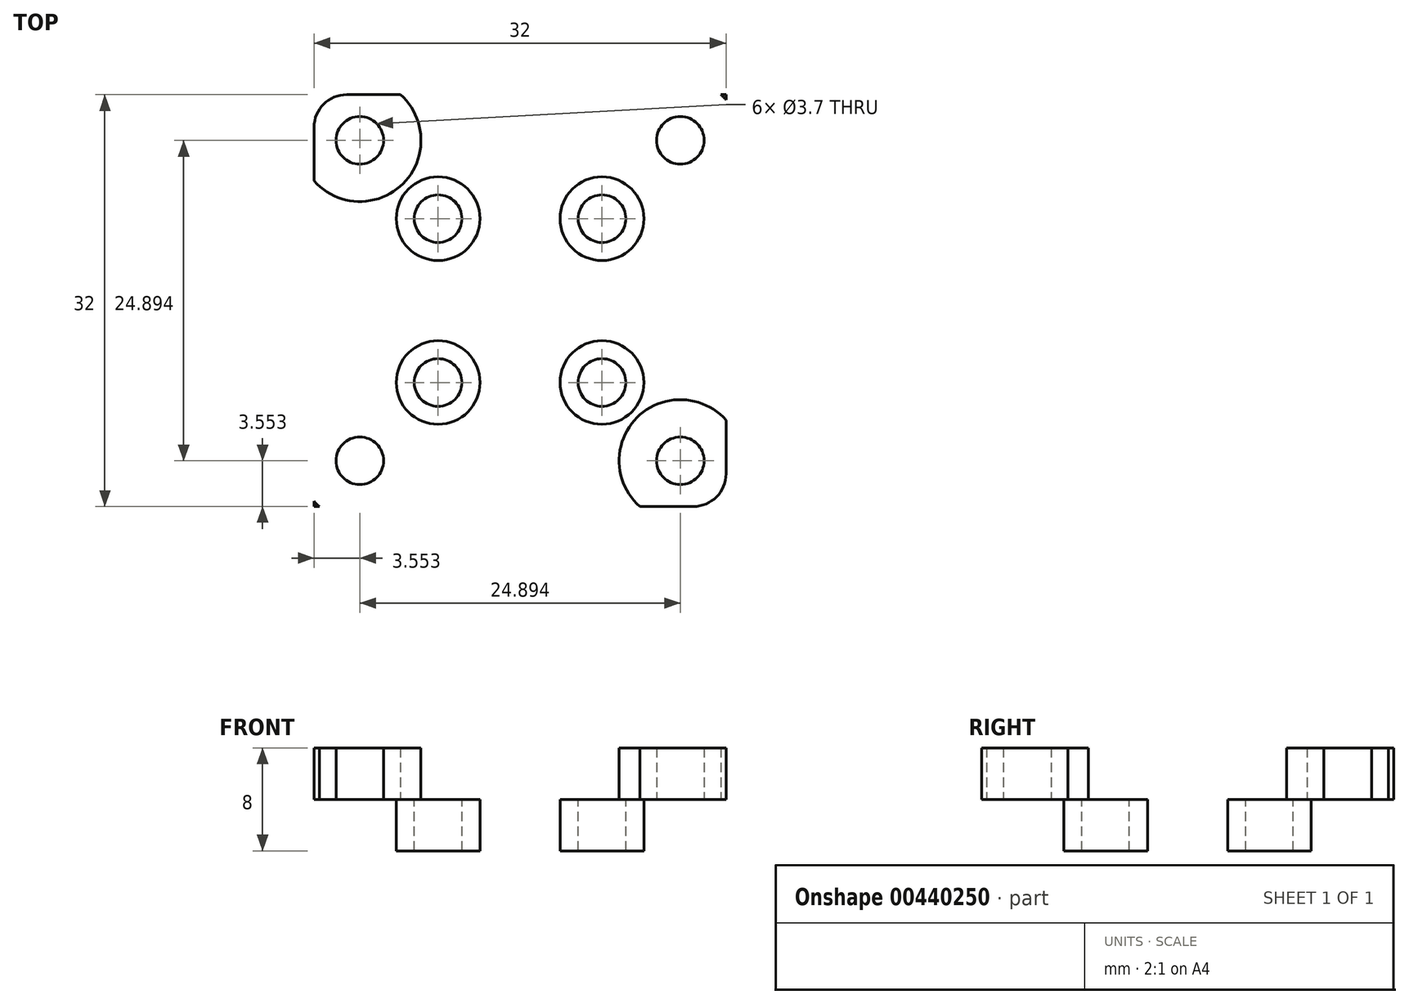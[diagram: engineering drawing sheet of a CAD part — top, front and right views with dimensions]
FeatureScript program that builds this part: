
annotation { "Feature Type Name" : "Feature", "Feature Type Description" : "" }
export const myFeature = defineFeature(function(context is Context, id is Id, definition is map)
    precondition{}
    {
        {
            var Q0;
            Q0=qCreatedBy(makeId("Top.planeOp"),FACE);
            var sketch = newSketch(context, id + "F0", { "sketchPlane" : qUnion([Q0])});
            skLineSegment(sketch, "E0.bottom", {"start": v(16, 16) * mm, "end": v(-16, 16) * mm});
            skLineSegment(sketch, "E0.top", {"start": v(16, -16) * mm, "end": v(-16, -16) * mm});
            skLineSegment(sketch, "E0.left", {"start": v(16, 16) * mm, "end": v(16, -16) * mm});
            skLineSegment(sketch, "E0.right", {"start": v(-16, 16) * mm, "end": v(-16, -16) * mm});
            skPoint(sketch, "E0.middle", {"position": v(0, 0) * mm});
            skCircle(sketch, "E1", {"center": v(-12.45, 12.45) * mm, "radius": 1.85 * mm});
            skCircle(sketch, "E2.MirrorC", {"center": v(12.45, 12.45) * mm, "radius": 1.85 * mm});
            skCircle(sketch, "E3.MirrorC", {"center": v(-12.45, -12.45) * mm, "radius": 1.85 * mm});
            skCircle(sketch, "E4.MirrorC", {"center": v(12.45, -12.45) * mm, "radius": 1.85 * mm});
            skCircle(sketch, "E5", {"center": v(-6.36, 6.36) * mm, "radius": 1.85 * mm});
            skCircle(sketch, "E6", {"center": v(6.36, 6.36) * mm, "radius": 1.85 * mm});
            skCircle(sketch, "E7", {"center": v(6.36, -6.36) * mm, "radius": 1.85 * mm});
            skCircle(sketch, "E8", {"center": v(-6.36, -6.36) * mm, "radius": 1.85 * mm});
            skCircle(sketch, "E9", {"center": v(-12.45, 12.45) * mm, "radius": 4.75 * mm});
            skCircle(sketch, "E10", {"center": v(12.45, 12.45) * mm, "radius": 4.75 * mm});
            skCircle(sketch, "E11", {"center": v(12.45, -12.45) * mm, "radius": 4.75 * mm});
            skCircle(sketch, "E12", {"center": v(-12.45, -12.45) * mm, "radius": 4.75 * mm});
            skCircle(sketch, "E13", {"center": v(-6.36, 6.36) * mm, "radius": 3.25 * mm});
            skCircle(sketch, "E14.MirrorC", {"center": v(6.36, 6.36) * mm, "radius": 3.25 * mm});
            skCircle(sketch, "E15.MirrorC", {"center": v(6.36, -6.36) * mm, "radius": 3.25 * mm});
            skCircle(sketch, "E16.MirrorC", {"center": v(-6.36, -6.36) * mm, "radius": 3.25 * mm});
            skSolve(sketch);
        }
        {
            var Q0;
            Q0=makeQuery(id+"F0.imprint","IMPRINT",FACE,{"disambiguationData":[TD([[makeQuery(id+"F0.imprint","IMPRINT",EDGE,{"derivedFrom":sQuery(id+"F0.wireOp",EDGE,"E13")}),-1.0]])]});
            var Q1;
            Q1=makeQuery(id+"F0.imprint","IMPRINT",FACE,{"disambiguationData":[TD([[makeQuery(id+"F0.imprint","IMPRINT",EDGE,{"derivedFrom":sQuery(id+"F0.wireOp",EDGE,"E1")}),-1.0]])]});
            var Q2;
            Q2=makeQuery(id+"F0.imprint","IMPRINT",FACE,{"disambiguationData":[TD([[makeQuery(id+"F0.imprint","IMPRINT",EDGE,{"derivedFrom":sQuery(id+"F0.wireOp",EDGE,"E2.MirrorC")}),1.0]])]});
            var Q3;
            Q3=makeQuery(id+"F0.imprint","IMPRINT",FACE,{"disambiguationData":[TD([[makeQuery(id+"F0.imprint","IMPRINT",EDGE,{"derivedFrom":sQuery(id+"F0.wireOp",EDGE,"E4.MirrorC")}),-1.0]])]});
            var Q4;
            Q4=makeQuery(id+"F0.imprint","IMPRINT",FACE,{"disambiguationData":[TD([[makeQuery(id+"F0.imprint","IMPRINT",EDGE,{"derivedFrom":sQuery(id+"F0.wireOp",EDGE,"E3.MirrorC")}),1.0]])]});
            var Q5;
            {var subQ0=sQuery(id+"F0.wireOp",EDGE,"E0.right");var subQ1=sQuery(id+"F0.wireOp",EDGE,"E0.bottom");var subQ2=makeQuery(id+"F0.imprint","INTERSECT",VERTEX,{"derivedFrom":[subQ1,subQ0]});Q5=makeQuery(id+"F0.imprint","IMPRINT",FACE,{"disambiguationData":[TD([[makeQuery(id+"F0.imprint","IMPRINT",EDGE,{"disambiguationData":[TD([[subQ2,1.0]])],"derivedFrom":subQ1}),1.0]])]});}
            var Q6;
            {var subQ0=sQuery(id+"F0.wireOp",EDGE,"E0.left");var subQ1=sQuery(id+"F0.wireOp",EDGE,"E0.bottom");var subQ2=makeQuery(id+"F0.imprint","INTERSECT",VERTEX,{"derivedFrom":[subQ1,subQ0]});Q6=makeQuery(id+"F0.imprint","IMPRINT",FACE,{"disambiguationData":[TD([[makeQuery(id+"F0.imprint","IMPRINT",EDGE,{"disambiguationData":[TD([[subQ2,-1.0]])],"derivedFrom":subQ1}),1.0]])]});}
            var Q7;
            {var subQ0=sQuery(id+"F0.wireOp",EDGE,"E0.left");var subQ1=sQuery(id+"F0.wireOp",EDGE,"E0.top");var subQ2=makeQuery(id+"F0.imprint","INTERSECT",VERTEX,{"derivedFrom":[subQ1,subQ0]});Q7=makeQuery(id+"F0.imprint","IMPRINT",FACE,{"disambiguationData":[TD([[makeQuery(id+"F0.imprint","IMPRINT",EDGE,{"disambiguationData":[TD([[subQ2,-1.0]])],"derivedFrom":subQ1}),-1.0]])]});}
            var Q8;
            {var subQ0=sQuery(id+"F0.wireOp",EDGE,"E0.right");var subQ1=sQuery(id+"F0.wireOp",EDGE,"E0.top");var subQ2=makeQuery(id+"F0.imprint","INTERSECT",VERTEX,{"derivedFrom":[subQ1,subQ0]});Q8=makeQuery(id+"F0.imprint","IMPRINT",FACE,{"disambiguationData":[TD([[makeQuery(id+"F0.imprint","IMPRINT",EDGE,{"disambiguationData":[TD([[subQ2,1.0]])],"derivedFrom":subQ1}),-1.0]])]});}
            extrude(context, id + "F1", {"entities" : qUnion([Q0, Q1, Q2, Q3, Q4, Q5, Q6, Q7, Q8]), "depth" : 4 * mm});
        }
        {
            var Q0;
            Q0=makeQuery(id+"F0.imprint","IMPRINT",FACE,{"disambiguationData":[TD([[makeQuery(id+"F0.imprint","IMPRINT",EDGE,{"derivedFrom":sQuery(id+"F0.wireOp",EDGE,"E13")}),-1.0]])]});
            var Q1;
            Q1=makeQuery(id+"F0.imprint","IMPRINT",FACE,{"disambiguationData":[TD([[makeQuery(id+"F0.imprint","IMPRINT",EDGE,{"derivedFrom":sQuery(id+"F0.wireOp",EDGE,"E8")}),-1.0]])]});
            var Q2;
            Q2=makeQuery(id+"F0.imprint","IMPRINT",FACE,{"disambiguationData":[TD([[makeQuery(id+"F0.imprint","IMPRINT",EDGE,{"derivedFrom":sQuery(id+"F0.wireOp",EDGE,"E7")}),-1.0]])]});
            var Q3;
            Q3=makeQuery(id+"F0.imprint","IMPRINT",FACE,{"disambiguationData":[TD([[makeQuery(id+"F0.imprint","IMPRINT",EDGE,{"derivedFrom":sQuery(id+"F0.wireOp",EDGE,"E6")}),-1.0]])]});
            var Q4;
            Q4=makeQuery(id+"F0.imprint","IMPRINT",FACE,{"disambiguationData":[TD([[makeQuery(id+"F0.imprint","IMPRINT",EDGE,{"derivedFrom":sQuery(id+"F0.wireOp",EDGE,"E5")}),-1.0]])]});
            extrude(context, id + "F2", {"entities" : qUnion([Q0, Q1, Q2, Q3, Q4]), "operationType" : NewBodyOperationType.ADD, "oppositeDirection" : true, "depth" : 4 * mm});
        }
        {
            var Q0;
            Q0=makeQuery(id+"F1.opExtrude","SWEPT_EDGE",EDGE,{"disambiguationData":[OSD([sQuery(id+"F0.wireOp",EDGE,"E0.bottom"),sQuery(id+"F0.wireOp",EDGE,"E0.left")])]});
            var Q1;
            Q1=makeQuery(id+"F1.opExtrude","SWEPT_EDGE",EDGE,{"disambiguationData":[OSD([sQuery(id+"F0.wireOp",EDGE,"E0.bottom"),sQuery(id+"F0.wireOp",EDGE,"E0.right")])]});
            var Q2;
            Q2=makeQuery(id+"F1.opExtrude","SWEPT_EDGE",EDGE,{"disambiguationData":[OSD([sQuery(id+"F0.wireOp",EDGE,"E0.top"),sQuery(id+"F0.wireOp",EDGE,"E0.right")])]});
            var Q3;
            Q3=makeQuery(id+"F1.opExtrude","SWEPT_EDGE",EDGE,{"disambiguationData":[OSD([sQuery(id+"F0.wireOp",EDGE,"E0.top"),sQuery(id+"F0.wireOp",EDGE,"E0.left")])]});
            fillet(context, id + "F3", {"entities" : qUnion([Q0, Q1, Q2, Q3]), "radius" : 2.54 * mm, "tangentPropagation" : true, "allowEdgeOverflow" : false});
        }
    });
